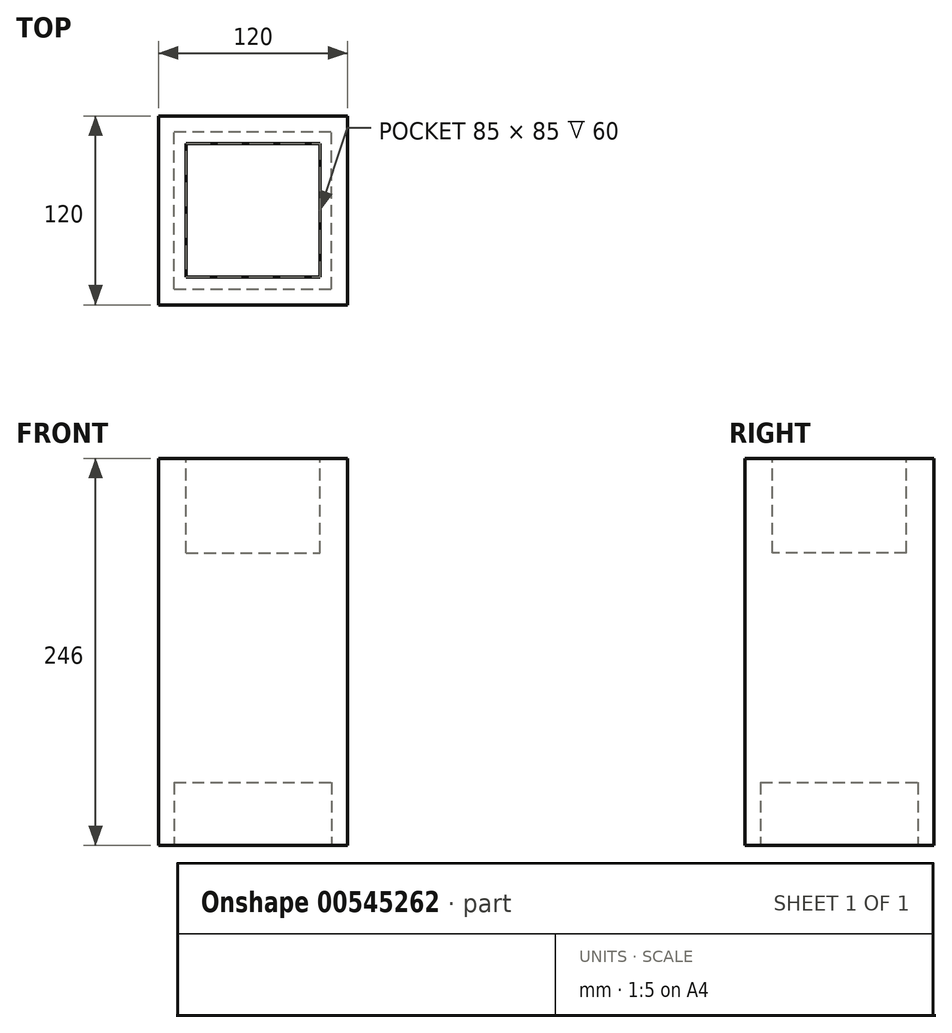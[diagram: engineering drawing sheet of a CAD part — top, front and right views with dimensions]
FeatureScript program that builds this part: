
annotation { "Feature Type Name" : "Feature", "Feature Type Description" : "" }
export const myFeature = defineFeature(function(context is Context, id is Id, definition is map)
    precondition{}
    {
        {
            var Q0;
            Q0=qCreatedBy(makeId("Top.planeOp"),FACE);
            var sketch = newSketch(context, id + "F0", { "sketchPlane" : qUnion([Q0])});
            skLineSegment(sketch, "E0.bottom", {"start": v(0, 0) * mm, "end": v(120, 0) * mm});
            skLineSegment(sketch, "E0.top", {"start": v(0, 120) * mm, "end": v(120, 120) * mm});
            skLineSegment(sketch, "E0.left", {"start": v(0, 0) * mm, "end": v(0, 120) * mm});
            skLineSegment(sketch, "E0.right", {"start": v(120, 0) * mm, "end": v(120, 120) * mm});
            skSolve(sketch);
        }
        {
            var Q0;
            Q0=makeQuery(id+"F0.imprint","IMPRINT",FACE,{"disambiguationData":[TD([[makeQuery(id+"F0.imprint","IMPRINT",EDGE,{"derivedFrom":sQuery(id+"F0.wireOp",EDGE,"E0.bottom")}),1.0]])]});
            extrude(context, id + "F1", {"entities" : qUnion([Q0]), "depth" : 246 * mm, "offsetDistance" : 25 * mm});
        }
        {
            var Q0;
            Q0=makeQuery(id+"F1.opExtrude","CAP_FACE",FACE,{"disambiguationData":[OSD([sQuery(id+"F0.wireOp",EDGE,"E0.bottom"),sQuery(id+"F0.wireOp",EDGE,"E0.top"),sQuery(id+"F0.wireOp",EDGE,"E0.left"),sQuery(id+"F0.wireOp",EDGE,"E0.right")])],"isStart":true});
            var sketch = newSketch(context, id + "F2", { "sketchPlane" : qUnion([Q0])});
            skLineSegment(sketch, "E1.bottom", {"start": v(0, 0) * mm, "end": v(120, 0) * mm});
            skLineSegment(sketch, "E1.top", {"start": v(0, -120) * mm, "end": v(120, -120) * mm});
            skLineSegment(sketch, "E1.left", {"start": v(0, 0) * mm, "end": v(0, -120) * mm});
            skLineSegment(sketch, "E1.right", {"start": v(120, 0) * mm, "end": v(120, -120) * mm});
            skLineSegment(sketch, "E2.bottom", {"start": v(10, -10) * mm, "end": v(110, -10) * mm});
            skLineSegment(sketch, "E2.top", {"start": v(10, -110) * mm, "end": v(110, -110) * mm});
            skLineSegment(sketch, "E2.left", {"start": v(10, -10) * mm, "end": v(10, -110) * mm});
            skLineSegment(sketch, "E2.right", {"start": v(110, -10) * mm, "end": v(110, -110) * mm});
            skSolve(sketch);
        }
        {
            var Q0;
            Q0=makeQuery(id+"F2.imprint","IMPRINT",FACE,{"disambiguationData":[TD([[makeQuery(id+"F2.imprint","IMPRINT",EDGE,{"derivedFrom":sQuery(id+"F2.wireOp",EDGE,"E2.bottom")}),-1.0]])]});
            extrude(context, id + "F3", {"entities" : qUnion([Q0]), "operationType" : NewBodyOperationType.REMOVE, "oppositeDirection" : true, "depth" : 40 * mm, "offsetDistance" : 25 * mm});
        }
        {
            var Q0;
            Q0=makeQuery(id+"F1.opExtrude","CAP_FACE",FACE,{"disambiguationData":[OSD([sQuery(id+"F0.wireOp",EDGE,"E0.bottom"),sQuery(id+"F0.wireOp",EDGE,"E0.top"),sQuery(id+"F0.wireOp",EDGE,"E0.left"),sQuery(id+"F0.wireOp",EDGE,"E0.right")])],"isStart":false});
            var sketch = newSketch(context, id + "F4", { "sketchPlane" : qUnion([Q0])});
            skLineSegment(sketch, "E3.bottom", {"start": v(0, 120) * mm, "end": v(120, 120) * mm});
            skLineSegment(sketch, "E3.top", {"start": v(0, 0) * mm, "end": v(120, 0) * mm});
            skLineSegment(sketch, "E3.left", {"start": v(0, 120) * mm, "end": v(0, 0) * mm});
            skLineSegment(sketch, "E3.right", {"start": v(120, 120) * mm, "end": v(120, 0) * mm});
            skLineSegment(sketch, "E4.bottom", {"start": v(17.5, 102.5) * mm, "end": v(102.5, 102.5) * mm});
            skLineSegment(sketch, "E4.top", {"start": v(17.5, 17.5) * mm, "end": v(102.5, 17.5) * mm});
            skLineSegment(sketch, "E4.left", {"start": v(17.5, 102.5) * mm, "end": v(17.5, 17.5) * mm});
            skLineSegment(sketch, "E4.right", {"start": v(102.5, 102.5) * mm, "end": v(102.5, 17.5) * mm});
            skLineSegment(sketch, "E5", {"start": v(60, 60) * mm, "end": v(102.5, 17.5) * mm, "construction": true});
            skLineSegment(sketch, "E6", {"start": v(60, 60) * mm, "end": v(102.5, 102.5) * mm, "construction": true});
            skLineSegment(sketch, "E7", {"start": v(60, 60) * mm, "end": v(120, 0) * mm, "construction": true});
            skLineSegment(sketch, "E8.trimOffspring", {"start": v(60, 60) * mm, "end": v(120, 120) * mm, "construction": true});
            skSolve(sketch);
        }
        {
            var Q0;
            Q0=makeQuery(id+"F4.imprint","IMPRINT",FACE,{"disambiguationData":[TD([[makeQuery(id+"F4.imprint","IMPRINT",EDGE,{"derivedFrom":sQuery(id+"F4.wireOp",EDGE,"E4.bottom")}),-1.0]])]});
            extrude(context, id + "F5", {"entities" : qUnion([Q0]), "operationType" : NewBodyOperationType.REMOVE, "oppositeDirection" : true, "depth" : 60 * mm, "offsetDistance" : 25 * mm});
        }
    });
